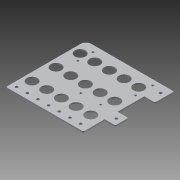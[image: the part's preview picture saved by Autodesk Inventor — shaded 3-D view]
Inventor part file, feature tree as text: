
AUTODESK INVENTOR PART (.ipt)
format: ipt  version: 2013 (Build 170138000, 138)  size: 190,976 bytes
history: native  units: in
note: dims shown in document units (in); Inventor stores cm internally (conversion verified against a paired STEP export)
features: reference x11, extrude x1, fillet x1, sketch x1
ambient origin geometry x8: Origin, YZ Plane, XZ Plane, XY Plane, X Axis, Y Axis, Z Axis, Center Point
bodies: Solid1 (feature_tree)
feature tree (14):
  extrude  "Extrusion1"  Depth=0.2in
  fillet  "Fillet1"  Radius=0.125in
  sketch  "Sketch1"  dims[d8=1.86in d9=0.2in d12=0.125in d13=0.0in d20=0.125in d21=1.61in d23=0.2in d24=0.5in d26=8.25in d29=1.375in d30=3.0in d31=7.5in d35=1.42in d37=1.25in d39=5.5105in d40=0.5in d41=1.0in d43=2.0in d44=1.9685in d46=1.375in d47=1.1811in d49=2.25in]
  reference  "Reference7"
  reference  "Reference8"
  reference  "Reference9"
  reference  "Reference10"
  reference  "Reference11"
  reference  "Reference12"
  reference  "Reference13"
  reference  "Reference14"
  reference  "Reference15"
  reference  "Reference16"
  reference  "Reference17"
